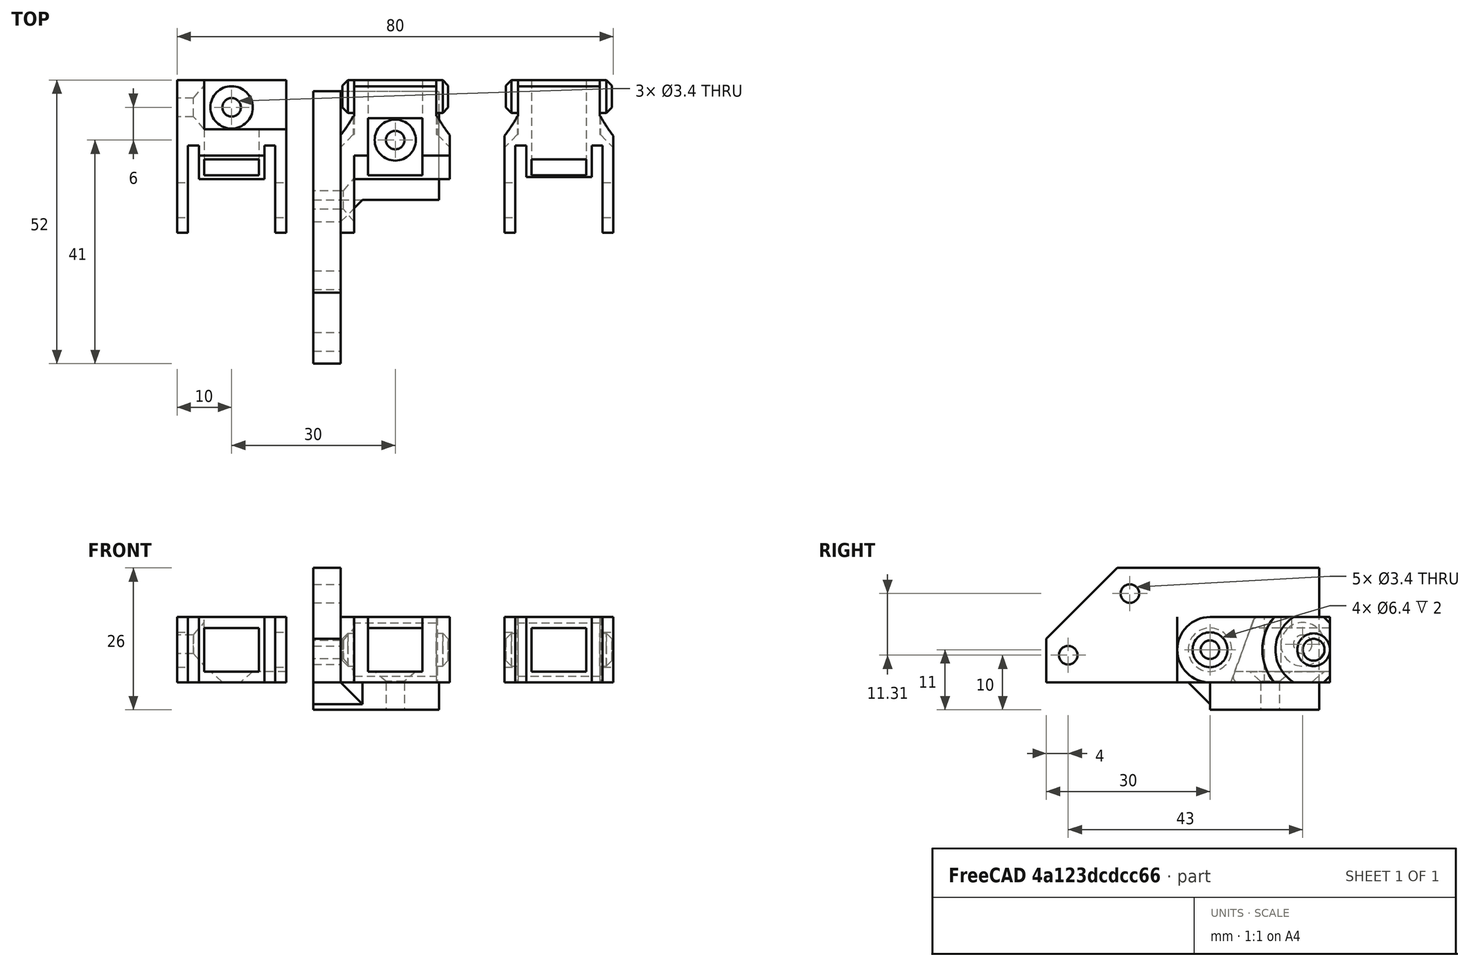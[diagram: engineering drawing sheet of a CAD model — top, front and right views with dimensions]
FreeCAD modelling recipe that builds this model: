
FCSTD DOCUMENT  (FreeCAD 0.14R3692 (Git))
Label: new-cable-chain
License: CC-BY 3.0
LicenseURL: http://creativecommons.org/licenses/by/3.0/
objects: Part::Cut×30, Part::Box×25, Part::Cylinder×15, Part::Fuse×15, Part::Chamfer×10, Part::Cone×3, Part::Fillet×2, Mesh::Feature×1
note: 100 computed .brp shape members not serialized (recipe doc carries the construction recipe); baked Part::Feature solids carry a one-line shape summary decoded from their .brp

FEATURE [Mesh::Feature] link_v1_2  label="link_v1.2"
  Placement = pos=(40,0,0) rot=(0,0,1;0rad)
FEATURE [Part::Box] Box  label="Cube"
  Height = 25
  Length = 20
  Width = 12
FEATURE [Part::Cylinder] Cylinder
  Angle = 360
  Height = 20
  Placement = pos=(0,6,25) rot=(0,1,0;1.5708rad)
  Radius = 6
FEATURE [Part::Fuse] Fusion
  Base = -> Box
  Tool = -> Cylinder
FEATURE [Part::Box] Box001  label="Cube001"
  Height = 20
  Length = 2
  Placement = pos=(2,-1,15) rot=(0,0,1;0rad)
  Width = 15
FEATURE [Part::Box] Box002  label="Cube002"
  Height = 20
  Length = 2
  Placement = pos=(16,-1,15) rot=(0,0,1;0rad)
  Width = 15
FEATURE [Part::Cut] Cut
  Base = -> Fusion
  Tool = -> Box001
FEATURE [Part::Cut] Cut001
  Base = -> Cut
  Tool = -> Box002
FEATURE [Part::Cylinder] Cylinder001
  Angle = 360
  Height = 25
  Placement = pos=(-2,6,25) rot=(0,1,0;1.5708rad)
  Radius = 3.2
FEATURE [Part::Cut] Cut002
  Base = -> Cut001
  Tool = -> Cylinder001
FEATURE [Part::Box] Box003  label="Cube003"
  Height = 20
  Length = 15
  Placement = pos=(2.5,-5,23) rot=(-1,0,0;0.349066rad)
  Width = 20
FEATURE [Part::Cut] Cut003
  Base = -> Cut002
  Tool = -> Box003
FEATURE [Part::Fillet] Fillet
  Base = -> Cut003
  Edges = 1 edges r=1: [Edge25]
FEATURE [Part::Fillet] Fillet001
  Base = -> Fillet
  Edges = 1 edges r=1: [Edge45]
FEATURE [Part::Cylinder] Cylinder002
  Angle = 360
  Height = 19.4
  Placement = pos=(0.3,6,6) rot=(0,1,0;1.5708rad)
  Radius = 3
FEATURE [Part::Cylinder] Cylinder003
  Angle = 360
  Height = 5
  Placement = pos=(-2.5,6,6) rot=(0,1,0;1.5708rad)
  Radius = 7
FEATURE [Part::Cylinder] Cylinder004
  Angle = 360
  Height = 5
  Placement = pos=(17.5,6,6) rot=(0,1,0;1.5708rad)
  Radius = 7
FEATURE [Part::Cut] Cut004
  Base = -> Fillet001
  Tool = -> Cylinder003
FEATURE [Part::Cut] Cut005
  Base = -> Cut004
  Tool = -> Cylinder004
FEATURE [Part::Chamfer] Chamfer
  Base = -> Cut005
  Edges = 1 edges r=2.4: [Edge58]
FEATURE [Part::Chamfer] Chamfer001
  Base = -> Chamfer
  Edges = 1 edges r=2.4: [Edge75]
FEATURE [Part::Fuse] Fusion001
  Base = -> Cylinder002
  Tool = -> Chamfer001
FEATURE [Part::Box] Box004  label="Cube004"
  Height = 10
  Length = 30
  Placement = pos=(-5,0,-10) rot=(1,0,0;0.785398rad)
  Width = 10
FEATURE [Part::Box] Box005  label="Cube005"
  Height = 10
  Length = 30
  Placement = pos=(-5,12,-10) rot=(1,0,0;0.785398rad)
  Width = 10
FEATURE [Part::Cut] Cut006
  Base = -> Fusion001
  Tool = -> Box004
FEATURE [Part::Cut] Cut007
  Base = -> Cut006
  Tool = -> Box005
FEATURE [Part::Box] Box006  label="Cube006"
  Height = 30
  Length = 10
  Placement = pos=(5,2,-1) rot=(0,0,1;0rad)
  Width = 8
FEATURE [Part::Cut] Cut008
  Base = -> Cut007
  Tool = -> Box006
FEATURE [Part::Box] Box007  label="Cube007"
  Height = 10
  Length = 30
  Placement = pos=(-1,-1,-7) rot=(0,0,1;0rad)
  Width = 15
FEATURE [Part::Cut] Cut009
  Base = -> Cut008
  Tool = -> Box007
FEATURE [Part::Chamfer] Chamfer002
  Base = -> Cut009
  Edges = 1 edges r=1: [Edge1]
FEATURE [Part::Chamfer] Chamfer003  label="link"
  Base = -> Chamfer002
  Edges = 1 edges r=1: [Edge94]
  Placement = pos=(30,0,0) rot=(1,0,0;1.5708rad)
FEATURE [Part::Cylinder] Cylinder005
  Angle = 360
  Height = 19.4
  Placement = pos=(0.3,6,6) rot=(0,1,0;1.5708rad)
  Radius = 3
FEATURE [Part::Box] Box008  label="Cube008"
  Height = 31
  Length = 20
  Width = 12
FEATURE [Part::Box] Box011  label="Cube011"
  Height = 20
  Length = 19
  Placement = pos=(2.5,-5,23) rot=(-1,0,0;0.349066rad)
  Width = 20
FEATURE [Part::Cylinder] Cylinder008
  Angle = 360
  Height = 5
  Placement = pos=(-2.5,6,6) rot=(0,1,0;1.5708rad)
  Radius = 7
FEATURE [Part::Cylinder] Cylinder009
  Angle = 360
  Height = 5
  Placement = pos=(17.5,6,6) rot=(0,1,0;1.5708rad)
  Radius = 7
FEATURE [Part::Box] Box012  label="Cube012"
  Height = 10
  Length = 30
  Placement = pos=(-5,0,-10) rot=(1,0,0;0.785398rad)
  Width = 10
FEATURE [Part::Box] Box013  label="Cube013"
  Height = 10
  Length = 30
  Placement = pos=(-5,12,-10) rot=(1,0,0;0.785398rad)
  Width = 10
FEATURE [Part::Box] Box014  label="Cube014"
  Height = 30
  Length = 10
  Placement = pos=(5,2,-1) rot=(0,0,1;0rad)
  Width = 8
FEATURE [Part::Box] Box015  label="Cube015"
  Height = 10
  Length = 30
  Placement = pos=(-1,-1,-7) rot=(0,0,1;0rad)
  Width = 15
FEATURE [Part::Cut] Cut010
  Base = -> Box008
  Tool = -> Box011
FEATURE [Part::Cut] Cut011
  Base = -> Cut010
  Tool = -> Cylinder008
FEATURE [Part::Cut] Cut012
  Base = -> Cut011
  Tool = -> Cylinder009
FEATURE [Part::Cut] Cut013
  Base = -> Cut012
  Tool = -> Box012
FEATURE [Part::Cut] Cut014
  Base = -> Cut013
  Tool = -> Box013
FEATURE [Part::Cut] Cut015
  Base = -> Cut014
  Tool = -> Box015
FEATURE [Part::Fuse] Fusion002
  Base = -> Cylinder005
  Tool = -> Cut015
FEATURE [Part::Box] Box016  label="Cube016"
  Height = 30
  Length = 10
  Placement = pos=(5,2,10) rot=(0,0,1;0rad)
  Width = 28
FEATURE [Part::Cut] Cut016
  Base = -> Fusion002
  Tool = -> Box014
FEATURE [Part::Cut] Cut017
  Base = -> Cut016
  Tool = -> Box016
FEATURE [Part::Chamfer] Chamfer004
  Base = -> Cut017
  Edges = 1 edges r=1: [Edge1]
FEATURE [Part::Chamfer] Chamfer005
  Base = -> Chamfer004
  Edges = 1 edges r=1: [Edge75]
FEATURE [Part::Cylinder] Cylinder010
  Angle = 360
  Height = 10
  Radius = 1.7
FEATURE [Part::Cone] Cone
  Angle = 360
  Height = 2
  Radius1 = 4
  Radius2 = 1.7
FEATURE [Part::Fuse] Fusion003  label="M3-screw"
  Base = -> Cylinder010
  Placement = pos=(10,2.2,14) rot=(1,0,0;1.5708rad)
  Tool = -> Cone
FEATURE [Part::Fuse] Fusion005  label="M3-screw002"
  Base = -> Cylinder010
  Placement = pos=(2.5,6,25) rot=(0,-1,0;1.5708rad)
  Tool = -> Cone
FEATURE [Part::Chamfer] Chamfer006
  Base = -> Chamfer005
  Edges = 1 edges r=2.3: [Edge52]
FEATURE [Part::Chamfer] Chamfer007
  Base = -> Chamfer006
  Edges = 1 edges r=2.3: [Edge43]
FEATURE [Part::Cut] Cut018
  Base = -> Chamfer007
  Tool = -> Fusion003
FEATURE [Part::Cut] Cut019  label="end-clip-1"
  Base = -> Cut018
  Placement = pos=(0,0,0) rot=(1,0,0;1.5708rad)
  Tool = -> Fusion005
FEATURE [Part::Box] Box017  label="Cube017"
  Height = 10
  Length = 30
  Placement = pos=(-1,-1,-7) rot=(0,0,1;0rad)
  Width = 15
FEATURE [Part::Cylinder] Cylinder011
  Angle = 360
  Height = 25
  Placement = pos=(-2,6,25) rot=(0,1,0;1.5708rad)
  Radius = 3.2
FEATURE [Part::Box] Box019  label="Cube019"
  Height = 25
  Length = 20
  Width = 12
FEATURE [Part::Box] Box021  label="Cube021"
  Height = 20
  Length = 2
  Placement = pos=(16,-1,15) rot=(0,0,1;0rad)
  Width = 15
FEATURE [Part::Cylinder] Cylinder013
  Angle = 360
  Height = 20
  Placement = pos=(0,6,25) rot=(0,1,0;1.5708rad)
  Radius = 6
FEATURE [Part::Box] Box022  label="Cube022"
  Height = 20
  Length = 2
  Placement = pos=(2,-1,15) rot=(0,0,1;0rad)
  Width = 15
FEATURE [Part::Box] Box023  label="Cube023"
  Height = 30
  Length = 10
  Placement = pos=(5,2,-1) rot=(0,0,1;0rad)
  Width = 8
FEATURE [Part::Box] Box024  label="Cube024"
  Height = 20
  Length = 15
  Placement = pos=(2.5,-5,23) rot=(-1,0,0;0.349066rad)
  Width = 20
FEATURE [Part::Fuse] Fusion006
  Base = -> Box019
  Tool = -> Cylinder013
FEATURE [Part::Cut] Cut020
  Base = -> Fusion006
  Tool = -> Box024
FEATURE [Part::Cut] Cut021
  Base = -> Cut020
  Tool = -> Box021
FEATURE [Part::Cut] Cut022
  Base = -> Cut021
  Tool = -> Box022
FEATURE [Part::Cut] Cut023
  Base = -> Cut022
  Tool = -> Box017
FEATURE [Part::Box] Box025  label="Cube025"
  Height = 30
  Length = 20
  Placement = pos=(5,2,-18) rot=(0,0,1;0rad)
  Width = 28
FEATURE [Part::Fuse] Fusion007
  Base = -> Box023
  Tool = -> Box025
FEATURE [Part::Cut] Cut024
  Base = -> Cut023
  Tool = -> Fusion007
FEATURE [Part::Cut] Cut025
  Base = -> Cut024
  Tool = -> Cylinder011
FEATURE [Part::Fuse] Fusion008  label="M3-screw003"
  Base = -> Cylinder010
  Placement = pos=(5,7,8) rot=(0,-1,0;1.5708rad)
  Tool = -> Cone
FEATURE [Part::Fuse] Fusion009  label="M3-screw004"
  Base = -> Cylinder010
  Placement = pos=(10,2.1,8) rot=(1,0,0;1.5708rad)
  Tool = -> Cone
FEATURE [Part::Cut] Cut026
  Base = -> Cut025
  Tool = -> Fusion008
FEATURE [Part::Cut] Cut027  label="end-clip-2"
  Base = -> Cut026
  Placement = pos=(-30,0,0) rot=(1,0,0;1.5708rad)
  Tool = -> Fusion009
FEATURE [Part::Cone] Cone001
  Angle = 360
  Height = 2
  Radius1 = 4
  Radius2 = 1.7
FEATURE [Part::Cylinder] Cylinder014
  Angle = 360
  Height = 30
  Radius = 1.7
FEATURE [Part::Fuse] Fusion010  label="M3-screw005"
  Base = -> Cylinder014
  Placement = pos=(10,2.2,14) rot=(1,0,0;1.5708rad)
  Tool = -> Cone001
FEATURE [Part::Cone] Cone002
  Angle = 360
  Height = 2
  Radius1 = 4
  Radius2 = 1.7
FEATURE [Part::Cylinder] Cylinder015
  Angle = 360
  Height = 30
  Radius = 1.7
FEATURE [Part::Fuse] Fusion011  label="M3-screw006"
  Base = -> Cylinder015
  Placement = pos=(2.5,6,25) rot=(0,-1,0;1.5708rad)
  Tool = -> Cone002
FEATURE [Part::Fuse] Fusion012  label="holes"
  Base = -> Fusion010
  Placement = pos=(0,0,0) rot=(1,0,0;1.5708rad)
  Tool = -> Fusion011
FEATURE [Part::Box] Box026  label="Cube026"
  Height = 21
  Length = 5
  Placement = pos=(-5,-55,0) rot=(0,0,1;0rad)
  Width = 50
FEATURE [Part::Box] Box027  label="Cube027"
  Height = 5
  Length = 23
  Placement = pos=(-5,-25,-5) rot=(0,0,1;0rad)
  Width = 20
FEATURE [Part::Cylinder] Cylinder016
  Angle = 360
  Height = 30
  Placement = pos=(-18,-41,5) rot=(0,1,0;1.5708rad)
  Radius = 1.7
FEATURE [Part::Cylinder] Cylinder017
  Angle = 360
  Height = 30
  Placement = pos=(-18,-29.69,16.31) rot=(0,1,0;1.5708rad)
  Radius = 1.7
FEATURE [Part::Box] Box028  label="Cube028"
  Height = 23
  Length = 14
  Placement = pos=(-10,-46,7) rot=(1,0,0;0.785398rad)
  Width = 22
FEATURE [Part::Fuse] Fusion013
  Base = -> Cylinder016
  Tool = -> Cylinder017
FEATURE [Part::Fuse] Fusion014
  Base = -> Box028
  Placement = pos=(0,-10,0) rot=(0,0,1;0rad)
  Tool = -> Fusion013
FEATURE [Part::Fuse] Fusion015
  Base = -> Box026
  Tool = -> Box027
FEATURE [Part::Cut] Cut028
  Base = -> Fusion015
  Tool = -> Fusion014
FEATURE [Part::Cut] Cut029
  Base = -> Cut028
  Tool = -> Fusion012
FEATURE [Part::Chamfer] Chamfer008
  Base = -> Cut029
  Edges = 1 edges r=4: [Edge22]
FEATURE [Part::Chamfer] Chamfer009  label="bracket"
  Base = -> Chamfer008
  Edges = 1 edges r=4: [Edge4]
